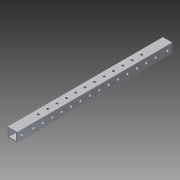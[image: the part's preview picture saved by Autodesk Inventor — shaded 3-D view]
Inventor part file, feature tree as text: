
AUTODESK INVENTOR PART (.ipt)
format: ipt  version: 2013 (Build 170138000, 138)  size: 168,448 bytes
history: native  units: in
note: dims shown in document units (in); Inventor stores cm internally (conversion verified against a paired STEP export)
features: extrude x3, sketch x3
ambient origin geometry x8: Origin, YZ Plane, XZ Plane, XY Plane, X Axis, Y Axis, Z Axis, Center Point
bodies: Solid1 (feature_tree)
feature tree (6):
  extrude  "Extrusion1"  Depth=1.0in
  extrude  "Extrusion2"  Depth=16.5in TaperAngle=0.0deg
  extrude  "Extrusion3"  Depth=0.26in
  sketch  "Sketch1"  dims[d0=1.0in d1=1.0in]
  sketch  "Sketch2"  dims[d2=0.125in d3=16.5in d4=0.0in]
  sketch  "Sketch3"  dims[d5=0.75in d7=0.26in d8=16.5in d9=0.0in d10=16.5in d11=6.2992in d13=1.0in d14=0.3937in d16=1.0in d18=0.75in d19=0.5in d20=0.26in d21=0.26in d22=0.5in d23=0.26in d25=0.75in d26=6.2992in d28=1.0in d29=0.3937in d31=1.0in d33=0.75in d34=1.0in d35=0.0in]
